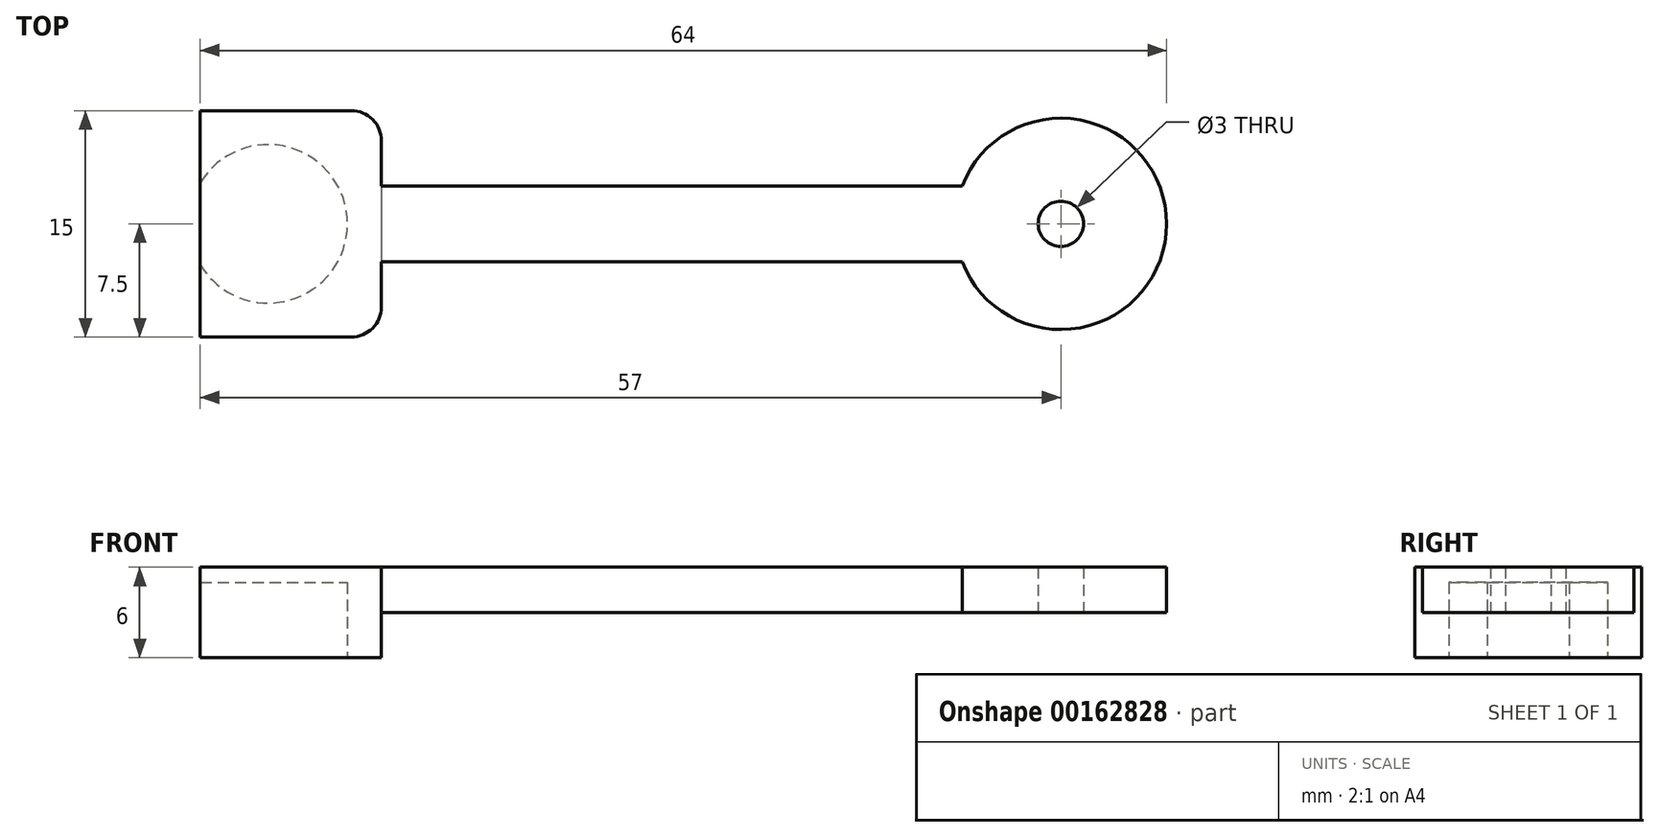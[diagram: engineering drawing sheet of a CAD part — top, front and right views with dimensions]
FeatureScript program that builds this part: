
annotation { "Feature Type Name" : "Feature", "Feature Type Description" : "" }
export const myFeature = defineFeature(function(context is Context, id is Id, definition is map)
    precondition{}
    {
        {
            var Q0;
            Q0=qCreatedBy(makeId("Top.planeOp"),FACE);
            var sketch = newSketch(context, id + "F0", { "sketchPlane" : qUnion([Q0])});
            skLineSegment(sketch, "E0.bottom", {"start": v(30, -2.5) * mm, "end": v(-30, -2.5) * mm});
            skLineSegment(sketch, "E0.top", {"start": v(30, 2.5) * mm, "end": v(-30, 2.5) * mm});
            skLineSegment(sketch, "E0.left", {"start": v(30, -2.5) * mm, "end": v(30, 2.5) * mm});
            skLineSegment(sketch, "E0.right", {"start": v(-30, -2.5) * mm, "end": v(-30, 2.5) * mm});
            skPoint(sketch, "E0.middle", {"position": v(0, 0) * mm});
            skSolve(sketch);
        }
        {
            var Q0;
            Q0=makeQuery(id+"F0.imprint","IMPRINT",FACE,{"disambiguationData":[TD([[makeQuery(id+"F0.imprint","IMPRINT",EDGE,{"derivedFrom":sQuery(id+"F0.wireOp",EDGE,"E0.bottom")}),-1.0]])]});
            extrude(context, id + "F1", {"entities" : qUnion([Q0]), "depth" : 3 * mm});
        }
        {
            var Q0;
            Q0=makeQuery(id+"F1.opExtrude","CAP_FACE",FACE,{"disambiguationData":[OSD([sQuery(id+"F0.wireOp",EDGE,"E0.bottom"),sQuery(id+"F0.wireOp",EDGE,"E0.top"),sQuery(id+"F0.wireOp",EDGE,"E0.left"),sQuery(id+"F0.wireOp",EDGE,"E0.right")])],"isStart":false});
            var sketch = newSketch(context, id + "F2", { "sketchPlane" : qUnion([Q0])});
            skLineSegment(sketch, "E1.bottom", {"start": v(-30, 7.5) * mm, "end": v(-15, 7.5) * mm});
            skLineSegment(sketch, "E1.top", {"start": v(-30, -7.5) * mm, "end": v(-15, -7.5) * mm});
            skLineSegment(sketch, "E1.left", {"start": v(-30, 7.5) * mm, "end": v(-30, -7.5) * mm});
            skLineSegment(sketch, "E1.right", {"start": v(-15, 7.5) * mm, "end": v(-15, -7.5) * mm});
            skPoint(sketch, "E2", {"position": v(-31.82, 0) * mm});
            skPoint(sketch, "E2.positionSnap0", {"position": v(-30, 0) * mm});
            skSolve(sketch);
        }
        {
            var Q0;
            {var subQ0=sQuery(id+"F2.wireOp",EDGE,"E1.bottom");Q0=makeQuery(id+"F2.imprint","IMPRINT",FACE,{"disambiguationData":[TD([[makeQuery(id+"F2.imprint","IMPRINT",EDGE,{"derivedFrom":subQ0}),-1.0]])]});}
            var Q1;
            {var subQ0=sQuery(id+"F2.wireOp",EDGE,"E1.left");var subQ1=makeQuery(id+"F1.opExtrude","CAP_EDGE",EDGE,{"disambiguationData":[OSD([sQuery(id+"F0.wireOp",EDGE,"E0.bottom")])],"isStart":false});var subQ2=makeQuery(id+"F2.imprint","INTERSECT",VERTEX,{"derivedFrom":[subQ1,subQ0]});var subQ3=makeQuery(id+"F1.opExtrude","CAP_EDGE",EDGE,{"disambiguationData":[OSD([sQuery(id+"F0.wireOp",EDGE,"E0.top")])],"isStart":false});var subQ4=makeQuery(id+"F2.imprint","INTERSECT",VERTEX,{"derivedFrom":[subQ3,subQ0]});Q1=makeQuery(id+"F2.imprint","IMPRINT",FACE,{"disambiguationData":[TD([[makeQuery(id+"F2.imprint","IMPRINT",EDGE,{"disambiguationData":[TD([[subQ2,-1.0],[subQ4,1.0]])],"derivedFrom":subQ0}),-1.0]])]});}
            var Q2;
            {var subQ0=sQuery(id+"F2.wireOp",EDGE,"E1.top");Q2=makeQuery(id+"F2.imprint","IMPRINT",FACE,{"disambiguationData":[TD([[makeQuery(id+"F2.imprint","IMPRINT",EDGE,{"derivedFrom":subQ0}),1.0]])]});}
            extrude(context, id + "F3", {"entities" : qUnion([Q0, Q1, Q2]), "operationType" : NewBodyOperationType.ADD, "oppositeDirection" : true, "depth" : 6 * mm});
        }
        {
            var Q0;
            Q0=makeQuery(id+"F3.opExtrude","CAP_FACE",FACE,{"disambiguationData":[OSD([sQuery(id+"F2.wireOp",EDGE,"E1.bottom"),sQuery(id+"F2.wireOp",EDGE,"E1.top"),sQuery(id+"F2.wireOp",EDGE,"E1.left"),sQuery(id+"F2.wireOp",EDGE,"E1.right")])],"isStart":false});
            var sketch = newSketch(context, id + "F4", { "sketchPlane" : qUnion([Q0])});
            skCircle(sketch, "E3", {"center": v(-22.5, 0) * mm, "radius": 5.25 * mm});
            skPoint(sketch, "E3.centerSnap0", {"position": v(-22.5, 7.5) * mm});
            skPoint(sketch, "E3.centerSnap1", {"position": v(-30, 0) * mm});
            skSolve(sketch);
        }
        {
            var Q0;
            Q0=makeQuery(id+"F4.imprint","IMPRINT",FACE,{"disambiguationData":[TD([[makeQuery(id+"F4.imprint","IMPRINT",EDGE,{"derivedFrom":sQuery(id+"F4.wireOp",EDGE,"E3")}),1.0]])]});
            extrude(context, id + "F5", {"entities" : qUnion([Q0]), "operationType" : NewBodyOperationType.REMOVE, "oppositeDirection" : true, "depth" : 5 * mm});
        }
        {
            var Q0;
            Q0=makeQuery(id+"F3.boolean.opBoolean","MERGE",FACE,{"derivedFrom":[makeQuery(id+"F1.opExtrude","SWEPT_FACE",FACE,{"disambiguationData":[OSD([sQuery(id+"F0.wireOp",EDGE,"E0.right")])]}),makeQuery(id+"F3.opExtrude","SWEPT_FACE",FACE,{"disambiguationData":[OSD([sQuery(id+"F2.wireOp",EDGE,"E1.left")])]})]});
            extrude(context, id + "F6", {"entities" : qUnion([Q0]), "operationType" : NewBodyOperationType.REMOVE, "oppositeDirection" : true, "depth" : 3 * mm});
        }
        {
            var Q0;
            Q0=makeQuery(id+"F1.opExtrude","CAP_FACE",FACE,{"disambiguationData":[OSD([sQuery(id+"F0.wireOp",EDGE,"E0.bottom"),sQuery(id+"F0.wireOp",EDGE,"E0.top"),sQuery(id+"F0.wireOp",EDGE,"E0.left"),sQuery(id+"F0.wireOp",EDGE,"E0.right")])],"isStart":true});
            var sketch = newSketch(context, id + "F7", { "sketchPlane" : qUnion([Q0])});
            skCircle(sketch, "E4", {"center": v(30, 0) * mm, "radius": 7 * mm});
            skSolve(sketch);
        }
        {
            var Q0;
            {var subQ5=makeQuery(id+"F1.opExtrude","CAP_EDGE",EDGE,{"disambiguationData":[OSD([sQuery(id+"F0.wireOp",EDGE,"E0.left")])],"isStart":true});Q0=makeQuery(id+"F7.imprint","IMPRINT",FACE,{"disambiguationData":[TD([[makeQuery(id+"F7.imprint","IMPRINT",EDGE,{"derivedFrom":subQ5}),1.0]])]});}
            var Q1;
            {var subQ5=makeQuery(id+"F1.opExtrude","CAP_EDGE",EDGE,{"disambiguationData":[OSD([sQuery(id+"F0.wireOp",EDGE,"E0.left")])],"isStart":true});Q1=makeQuery(id+"F7.imprint","IMPRINT",FACE,{"disambiguationData":[TD([[makeQuery(id+"F7.imprint","IMPRINT",EDGE,{"derivedFrom":subQ5}),-1.0]])]});}
            extrude(context, id + "F8", {"entities" : qUnion([Q0, Q1]), "operationType" : NewBodyOperationType.ADD, "oppositeDirection" : true, "depth" : 3 * mm});
        }
        {
            var Q0;
            Q0=makeQuery(id+"F8.boolean.opBoolean","MERGE",FACE,{"derivedFrom":[makeQuery(id+"F1.opExtrude","CAP_FACE",FACE,{"disambiguationData":[OSD([sQuery(id+"F0.wireOp",EDGE,"E0.bottom"),sQuery(id+"F0.wireOp",EDGE,"E0.top"),sQuery(id+"F0.wireOp",EDGE,"E0.left"),sQuery(id+"F0.wireOp",EDGE,"E0.right")])],"isStart":true}),makeQuery(id+"F8.opExtrude","CAP_FACE",FACE,{"disambiguationData":[OSD([sQuery(id+"F7.wireOp",EDGE,"E4")])],"isStart":true})]});
            var sketch = newSketch(context, id + "F9", { "sketchPlane" : qUnion([Q0])});
            skCircle(sketch, "E5", {"center": v(30, 0) * mm, "radius": 1.5 * mm});
            skSolve(sketch);
        }
        {
            var Q0;
            Q0=makeQuery(id+"F9.imprint","IMPRINT",FACE,{"disambiguationData":[TD([[makeQuery(id+"F9.imprint","IMPRINT",EDGE,{"derivedFrom":sQuery(id+"F9.wireOp",EDGE,"E5")}),1.0]])]});
            extrude(context, id + "F10", {"entities" : qUnion([Q0]), "operationType" : NewBodyOperationType.REMOVE, "oppositeDirection" : true, "depth" : 25 * mm});
        }
        {
            var Q0;
            Q0=makeQuery(id+"F3.opExtrude","SWEPT_EDGE",EDGE,{"disambiguationData":[OSD([sQuery(id+"F2.wireOp",EDGE,"E1.top"),sQuery(id+"F2.wireOp",EDGE,"E1.right")])]});
            var Q1;
            Q1=makeQuery(id+"F3.opExtrude","SWEPT_EDGE",EDGE,{"disambiguationData":[OSD([sQuery(id+"F2.wireOp",EDGE,"E1.bottom"),sQuery(id+"F2.wireOp",EDGE,"E1.right")])]});
            fillet(context, id + "F11", {"entities" : qUnion([Q0, Q1]), "radius" : 2 * mm, "tangentPropagation" : true, "allowEdgeOverflow" : false});
        }
    });
